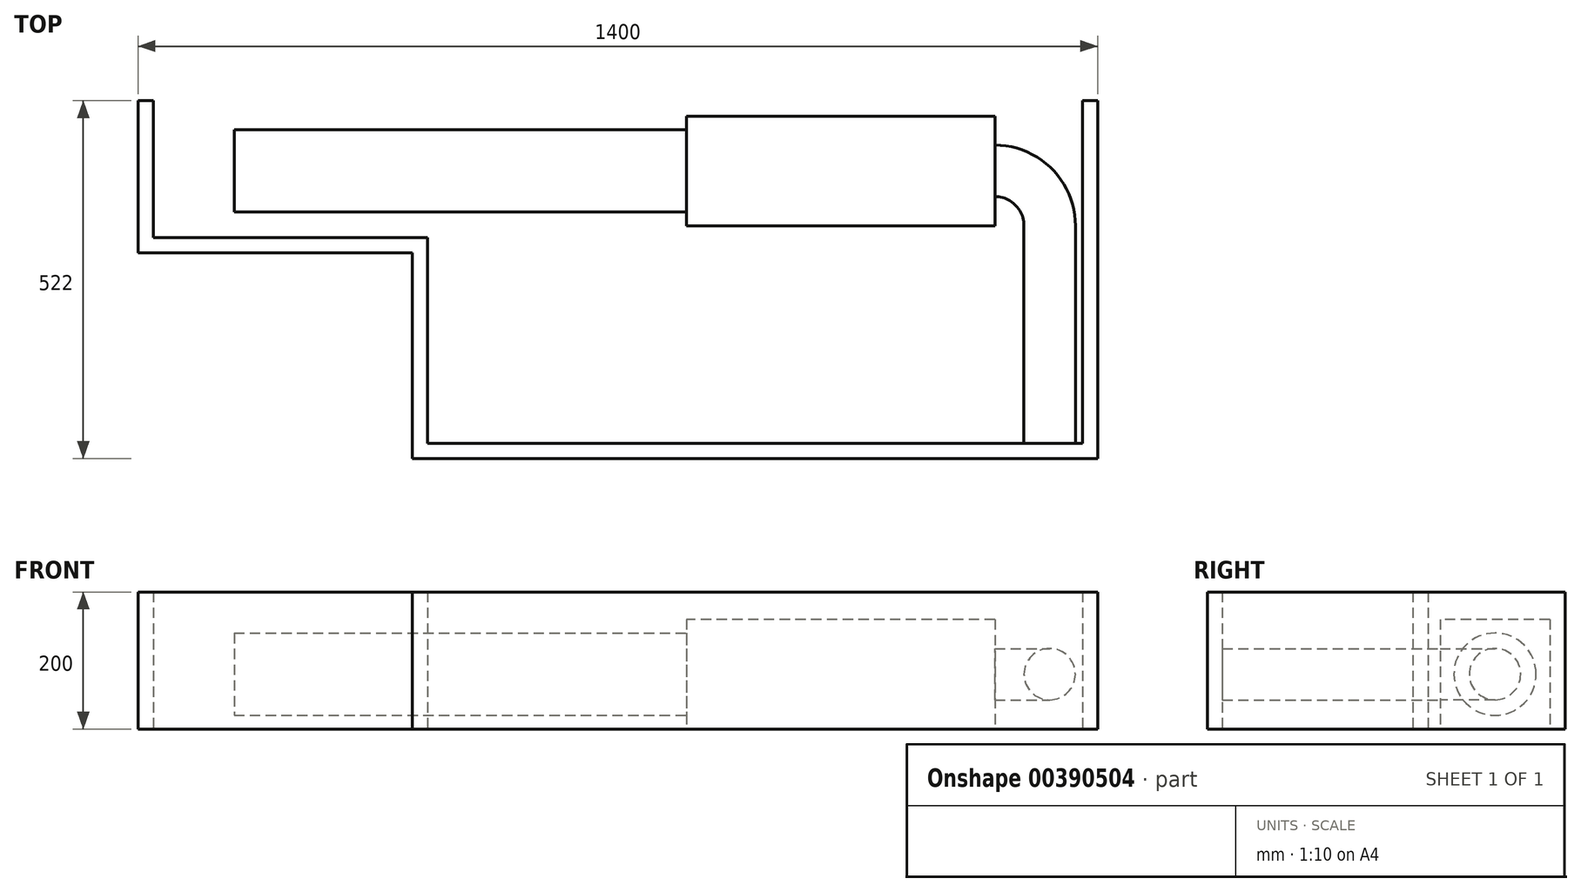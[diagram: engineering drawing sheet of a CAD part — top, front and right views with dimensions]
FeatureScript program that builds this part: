
annotation { "Feature Type Name" : "Feature", "Feature Type Description" : "" }
export const myFeature = defineFeature(function(context is Context, id is Id, definition is map)
    precondition{}
    {
        {
            var Q0;
            Q0=qCreatedBy(makeId("Top.planeOp"),FACE);
            var sketch = newSketch(context, id + "F0", { "sketchPlane" : qUnion([Q0])});
            skLineSegment(sketch, "E0.bottom", {"start": v(-150, -22.27) * mm, "end": v(-600, -22.27) * mm});
            skLineSegment(sketch, "E0.top", {"start": v(-150, -182.27) * mm, "end": v(-600, -182.27) * mm});
            skLineSegment(sketch, "E0.left", {"start": v(-150, -22.27) * mm, "end": v(-150, -182.27) * mm});
            skLineSegment(sketch, "E0.right", {"start": v(-600, -22.27) * mm, "end": v(-600, -182.27) * mm});
            skSolve(sketch);
        }
        {
            var Q0;
            Q0=makeQuery(id+"F0.imprint","IMPRINT",FACE,{"disambiguationData":[TD([[makeQuery(id+"F0.imprint","IMPRINT",EDGE,{"derivedFrom":sQuery(id+"F0.wireOp",EDGE,"E0.bottom")}),1.0]])]});
            extrude(context, id + "F1", {"entities" : qUnion([Q0]), "depth" : 160 * mm});
        }
        {
            var Q0;
            Q0=qCreatedBy(makeId("Top.planeOp"),FACE);
            var sketch = newSketch(context, id + "F2", { "sketchPlane" : qUnion([Q0])});
            skLineSegment(sketch, "E1", {"start": v(0, 0) * mm, "end": v(0, -522) * mm});
            skLineSegment(sketch, "E2", {"start": v(0, -522) * mm, "end": v(-1000, -522) * mm});
            skLineSegment(sketch, "E3", {"start": v(-978, -200) * mm, "end": v(-978, -500) * mm});
            skLineSegment(sketch, "E4", {"start": v(-978, -500) * mm, "end": v(-22, -500) * mm});
            skLineSegment(sketch, "E5", {"start": v(-22, -500) * mm, "end": v(-22, 0) * mm});
            skLineSegment(sketch, "E6", {"start": v(-22, 0) * mm, "end": v(0, 0) * mm});
            skLineSegment(sketch, "E7", {"start": v(-978, -200) * mm, "end": v(-1378, -200) * mm});
            skLineSegment(sketch, "E8", {"start": v(-1378, -200) * mm, "end": v(-1378, 0) * mm});
            skLineSegment(sketch, "E9", {"start": v(-1378, 0) * mm, "end": v(-1400, 0) * mm});
            skLineSegment(sketch, "E10", {"start": v(-1400, 0) * mm, "end": v(-1400, -222) * mm});
            skLineSegment(sketch, "E11", {"start": v(-1400, -222) * mm, "end": v(-1000, -222) * mm});
            skLineSegment(sketch, "E12", {"start": v(-1000, -222) * mm, "end": v(-1000, -522) * mm});
            skSolve(sketch);
        }
        {
            var Q0;
            Q0 = qSketchRegion(id + "F2", true);
            extrude(context, id + "F3", {"entities" : qUnion([Q0]), "depth" : 200 * mm});
        }
        {
            var Q0;
            Q0=makeQuery(id+"F1.opExtrude","SWEPT_FACE",FACE,{"disambiguationData":[OSD([sQuery(id+"F0.wireOp",EDGE,"E0.right")])]});
            var sketch = newSketch(context, id + "F4", { "sketchPlane" : qUnion([Q0])});
            skCircle(sketch, "E13", {"center": v(102.27, 80) * mm, "radius": 60 * mm});
            skPoint(sketch, "E13.centerSnap0", {"position": v(22.27, 80) * mm});
            skSolve(sketch);
        }
        {
            var Q0;
            Q0=makeQuery(id+"F4.imprint","IMPRINT",FACE,{"disambiguationData":[TD([[makeQuery(id+"F4.imprint","IMPRINT",EDGE,{"derivedFrom":sQuery(id+"F4.wireOp",EDGE,"E13")}),1.0]])]});
            extrude(context, id + "F5", {"entities" : qUnion([Q0]), "operationType" : NewBodyOperationType.ADD, "depth" : 660 * mm});
        }
        {
            var Q0;
            Q0=makeQuery(id+"F1.opExtrude","SWEPT_FACE",FACE,{"disambiguationData":[OSD([sQuery(id+"F0.wireOp",EDGE,"E0.left")])]});
            var sketch = newSketch(context, id + "F6", { "sketchPlane" : qUnion([Q0])});
            skCircle(sketch, "E14", {"center": v(-102.27, 80) * mm, "radius": 37.5 * mm});
            skPoint(sketch, "E14.centerSnap0", {"position": v(-182.27, 80) * mm});
            skSolve(sketch);
        }
        {
            var Q0;
            Q0=qCreatedBy(makeId("Top.planeOp"),FACE);
            var sketch = newSketch(context, id + "F7", { "sketchPlane" : qUnion([Q0])});
            skArc(sketch, "E15", {"start": v(-70, -182.27) * mm, "mid": v(-93.43, -125.7) * mm, "end": v(-150, -102.27) * mm});
            skSolve(sketch);
        }
        {
            var Q0;
            Q0 = qSketchRegion(id + "F6", true);
            var Q1;
            Q1 = qConstructionFilter(qBodyType(qCreatedBy(id + "F7" ,EDGE), BodyType.WIRE), ConstructionObject.NO);
            sweep(context, id + "F8", {"operationType" : NewBodyOperationType.ADD, "profiles" : qUnion([Q0]), "path" : qUnion([Q1])});
        }
        {
            var Q0;
            Q0=makeQuery(id+"F8.opSweep","CAP_FACE",FACE,{"disambiguationData":[OSD([sQuery(id+"F6.wireOp",EDGE,"E14"),sQuery(id+"F7.wireOp",VERTEX,"E15.start")])],"isStart":false});
            extrude(context, id + "F9", {"entities" : qUnion([Q0]), "operationType" : NewBodyOperationType.ADD, "endBound" : BoundingType.UP_TO_NEXT, "depth" : 25 * mm});
        }
    });
